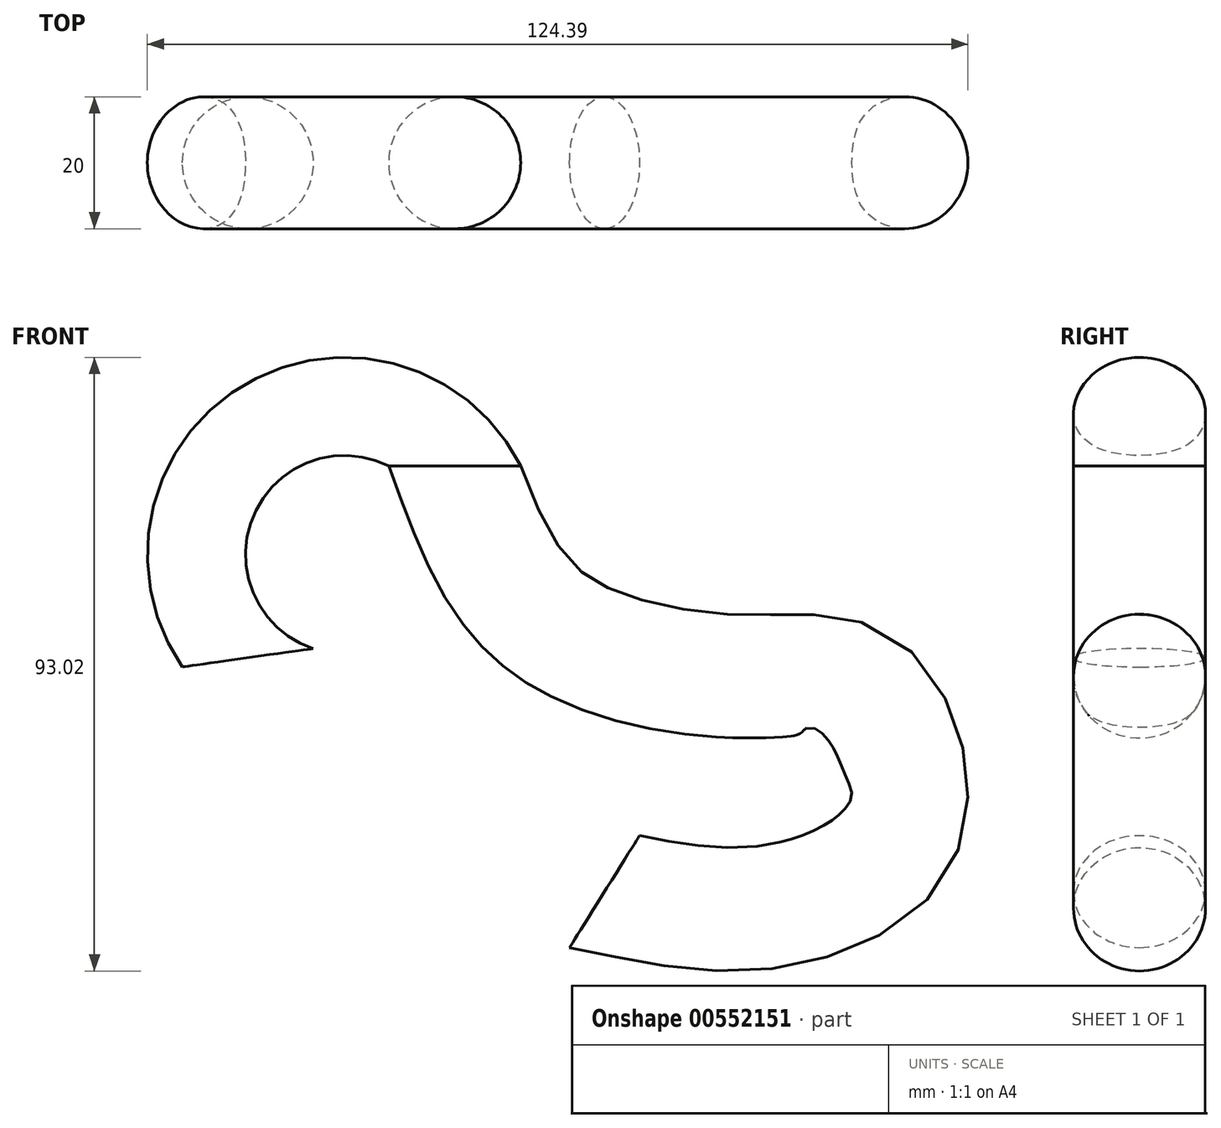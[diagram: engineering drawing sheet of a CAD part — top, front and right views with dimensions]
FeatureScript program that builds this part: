
annotation { "Feature Type Name" : "Feature", "Feature Type Description" : "" }
export const myFeature = defineFeature(function(context is Context, id is Id, definition is map)
    precondition{}
    {
        {
            var Q0;
            Q0=qCreatedBy(makeId("Top.planeOp"),FACE);
            var sketch = newSketch(context, id + "F0", { "sketchPlane" : qUnion([Q0])});
            skCircle(sketch, "E0", {"center": v(0, 0) * mm, "radius": 10 * mm});
            skSolve(sketch);
        }
        {
            var Q0;
            Q0=qCreatedBy(makeId("Front.planeOp"),FACE);
            var sketch = newSketch(context, id + "F1", { "sketchPlane" : qUnion([Q0])});
            skArc(sketch, "E1", {"start": v(0, 0) * mm, "mid": v(-31.27, 2.27) * mm, "end": v(-31.35, -29.08) * mm});
            skFitSpline(sketch, "E2", {"points": [v(0, 0) * mm, v(13.63, -23.17) * mm, v(42.26, -31.8) * mm, v(60.44, -33.63) * mm, v(67.7, -44.99) * mm, v(65.44, -58.16) * mm, v(46.8, -66.8) * mm, v(22.72, -64.53) * mm], "startDerivative": vector(60.4, -161.22) * mm, "endDerivative": vector(-154.6, 31.35) * mm});
            skSolve(sketch);
        }
        {
            var Q0;
            Q0=makeQuery(id+"F0.imprint","IMPRINT",FACE,{"disambiguationData":[TD([[makeQuery(id+"F0.imprint","IMPRINT",EDGE,{"derivedFrom":sQuery(id+"F0.wireOp",EDGE,"E0")}),1.0]])]});
            var Q1;
            Q1=sQuery(id+"F1.wireOp",EDGE,"E1");
            sweep(context, id + "F2", {"profiles" : qUnion([Q0]), "path" : qUnion([Q1])});
        }
        {
            var Q0;
            Q0=makeQuery(id+"F0.imprint","IMPRINT",FACE,{"disambiguationData":[TD([[makeQuery(id+"F0.imprint","IMPRINT",EDGE,{"derivedFrom":sQuery(id+"F0.wireOp",EDGE,"E0")}),1.0]])]});
            var Q1;
            Q1=sQuery(id+"F1.wireOp",EDGE,"E2");
            sweep(context, id + "F3", {"operationType" : NewBodyOperationType.ADD, "profiles" : qUnion([Q0]), "path" : qUnion([Q1])});
        }
    });
